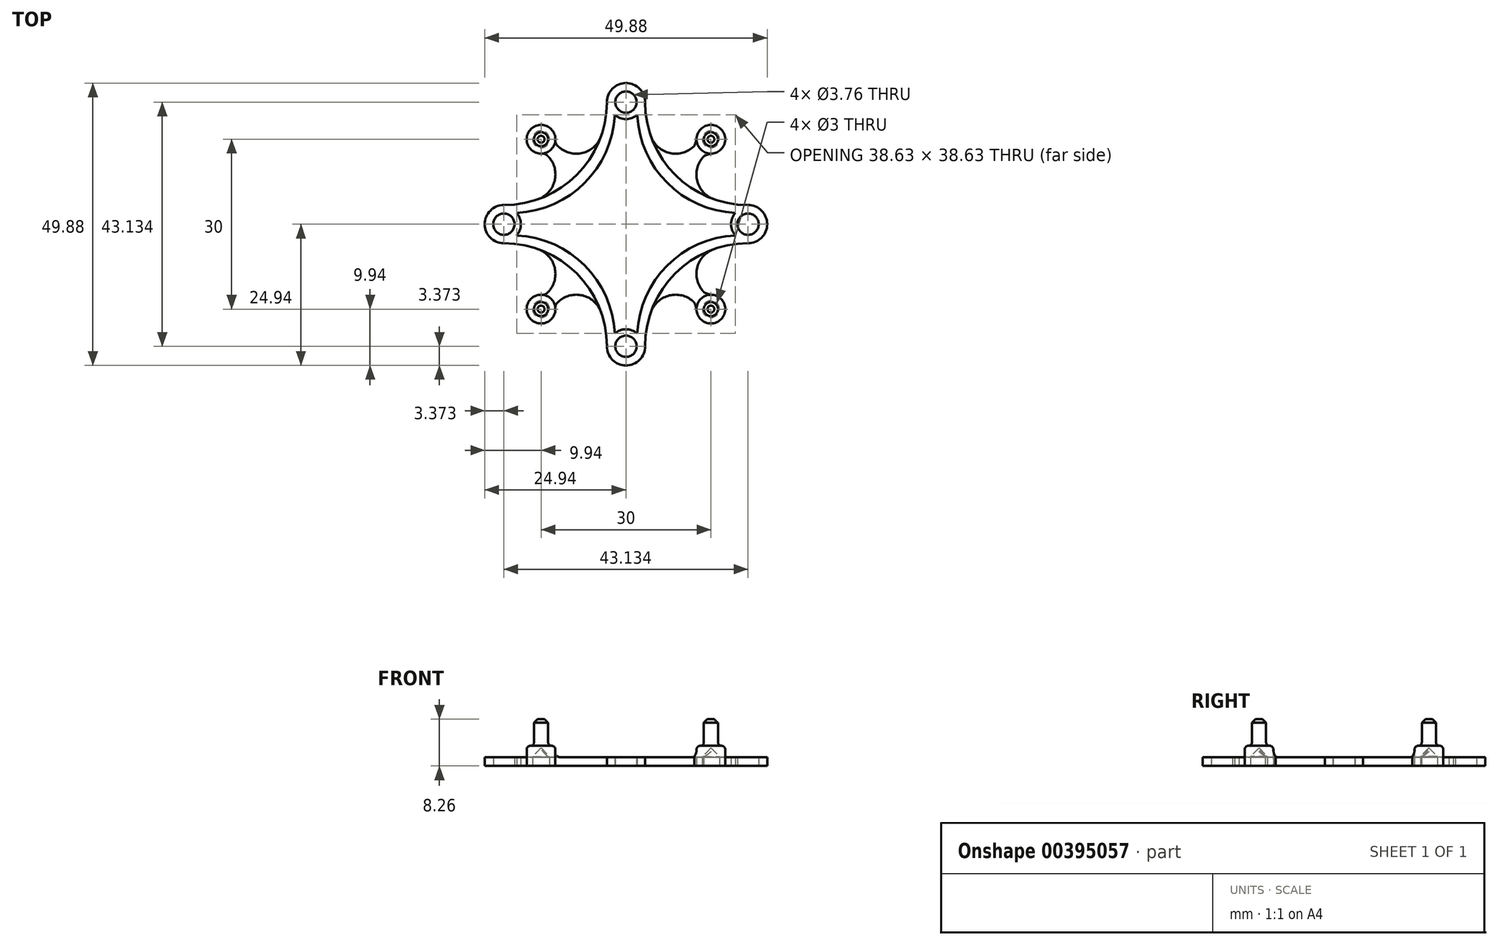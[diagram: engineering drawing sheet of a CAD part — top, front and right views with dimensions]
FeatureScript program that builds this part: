
annotation { "Feature Type Name" : "Feature", "Feature Type Description" : "" }
export const myFeature = defineFeature(function(context is Context, id is Id, definition is map)
    precondition{}
    {
        {
            var Q0;
            Q0=qCreatedBy(makeId("Top.planeOp"),FACE);
            var sketch = newSketch(context, id + "F0", { "sketchPlane" : qUnion([Q0])});
            skCircle(sketch, "E0", {"center": v(0, 21.57) * mm, "radius": 1.88 * mm});
            skCircle(sketch, "E1", {"center": v(-21.57, 0) * mm, "radius": 1.88 * mm});
            skCircle(sketch, "E2", {"center": v(0, -21.57) * mm, "radius": 1.88 * mm});
            skCircle(sketch, "E3", {"center": v(21.57, 0) * mm, "radius": 1.88 * mm});
            skLineSegment(sketch, "E4", {"start": v(0, 21.57) * mm, "end": v(0, -21.57) * mm, "construction": true});
            skLineSegment(sketch, "E5", {"start": v(21.57, 0) * mm, "end": v(-21.57, 0) * mm, "construction": true});
            skArc(sketch, "E6", {"start": v(3.38, 21.57) * mm, "mid": v(0, 24.94) * mm, "end": v(-3.38, 21.57) * mm});
            skArc(sketch, "E7", {"start": v(21.57, -3.38) * mm, "mid": v(24.94, 0) * mm, "end": v(21.57, 3.38) * mm});
            skArc(sketch, "E8", {"start": v(-3.38, -21.57) * mm, "mid": v(0, -24.94) * mm, "end": v(3.38, -21.57) * mm});
            skArc(sketch, "E9", {"start": v(-21.57, 3.38) * mm, "mid": v(-24.94, 0) * mm, "end": v(-21.57, -3.38) * mm});
            skArc(sketch, "E10", {"start": v(21.57, -3.38) * mm, "mid": v(8.7, -8.7) * mm, "end": v(3.38, -21.57) * mm});
            skArc(sketch, "E11", {"start": v(3.38, 21.57) * mm, "mid": v(8.7, 8.7) * mm, "end": v(21.57, 3.38) * mm});
            skArc(sketch, "E12", {"start": v(-21.57, 3.38) * mm, "mid": v(-8.7, 8.7) * mm, "end": v(-3.38, 21.57) * mm});
            skArc(sketch, "E13", {"start": v(-3.38, -21.57) * mm, "mid": v(-8.7, -8.7) * mm, "end": v(-21.57, -3.38) * mm});
            skArc(sketch, "E14", {"start": v(-1.98, 19.32) * mm, "mid": v(0, 18.57) * mm, "end": v(1.98, 19.32) * mm});
            skArc(sketch, "E15", {"start": v(-19.32, -1.98) * mm, "mid": v(-18.57, 0) * mm, "end": v(-19.32, 1.98) * mm});
            skArc(sketch, "E16", {"start": v(1.98, -19.32) * mm, "mid": v(0, -18.57) * mm, "end": v(-1.98, -19.32) * mm});
            skArc(sketch, "E17", {"start": v(19.32, 1.98) * mm, "mid": v(18.57, 0) * mm, "end": v(19.32, -1.98) * mm});
            skArc(sketch, "E18", {"start": v(19.32, -1.98) * mm, "mid": v(7.3, -7.3) * mm, "end": v(1.98, -19.32) * mm});
            skArc(sketch, "E19", {"start": v(1.98, 19.32) * mm, "mid": v(7.3, 7.3) * mm, "end": v(19.32, 1.98) * mm});
            skArc(sketch, "E20", {"start": v(-19.32, 1.98) * mm, "mid": v(-7.3, 7.3) * mm, "end": v(-1.98, 19.32) * mm});
            skArc(sketch, "E21", {"start": v(-1.98, -19.32) * mm, "mid": v(-7.3, -7.3) * mm, "end": v(-19.32, -1.98) * mm});
            skSolve(sketch);
        }
        {
            var Q0;
            Q0=makeQuery(id+"F0.imprint","IMPRINT",FACE,{"disambiguationData":[TD([[makeQuery(id+"F0.imprint","IMPRINT",EDGE,{"derivedFrom":sQuery(id+"F0.wireOp",EDGE,"E0")}),-1.0]])]});
            extrude(context, id + "F1", {"entities" : qUnion([Q0]), "depth" : 0.01 * mm});
        }
        {
            var Q0;
            Q0=qCreatedBy(makeId("Top.planeOp"),FACE);
            var sketch = newSketch(context, id + "F2", { "sketchPlane" : qUnion([Q0])});
            skLineSegment(sketch, "E22.bottom", {"start": v(15, -15) * mm, "end": v(-15, -15) * mm, "construction": true});
            skLineSegment(sketch, "E22.top", {"start": v(15, 15) * mm, "end": v(-15, 15) * mm, "construction": true});
            skLineSegment(sketch, "E22.left", {"start": v(15, -15) * mm, "end": v(15, 15) * mm, "construction": true});
            skLineSegment(sketch, "E22.right", {"start": v(-15, -15) * mm, "end": v(-15, 15) * mm, "construction": true});
            skPoint(sketch, "E22.middle", {"position": v(0, 0) * mm});
            skCircle(sketch, "E23", {"center": v(15, 15) * mm, "radius": 1.25 * mm});
            skCircle(sketch, "E24", {"center": v(15, -15) * mm, "radius": 1.25 * mm});
            skCircle(sketch, "E25", {"center": v(-15, 15) * mm, "radius": 1.25 * mm});
            skCircle(sketch, "E26", {"center": v(-15, -15) * mm, "radius": 1.25 * mm});
            skSolve(sketch);
        }
        {
            var Q0;
            Q0=makeQuery(id+"F2.imprint","IMPRINT",FACE,{"disambiguationData":[TD([[makeQuery(id+"F2.imprint","IMPRINT",EDGE,{"derivedFrom":sQuery(id+"F2.wireOp",EDGE,"E23")}),1.0]])]});
            var Q1;
            Q1=makeQuery(id+"F2.imprint","IMPRINT",FACE,{"disambiguationData":[TD([[makeQuery(id+"F2.imprint","IMPRINT",EDGE,{"derivedFrom":sQuery(id+"F2.wireOp",EDGE,"E25")}),1.0]])]});
            var Q2;
            Q2=makeQuery(id+"F2.imprint","IMPRINT",FACE,{"disambiguationData":[TD([[makeQuery(id+"F2.imprint","IMPRINT",EDGE,{"derivedFrom":sQuery(id+"F2.wireOp",EDGE,"E24")}),1.0]])]});
            var Q3;
            Q3=makeQuery(id+"F2.imprint","IMPRINT",FACE,{"disambiguationData":[TD([[makeQuery(id+"F2.imprint","IMPRINT",EDGE,{"derivedFrom":sQuery(id+"F2.wireOp",EDGE,"E26")}),1.0]])]});
            extrude(context, id + "F3", {"entities" : qUnion([Q0, Q1, Q2, Q3]), "depth" : 8.25 * mm});
        }
        {
            var Q0;
            Q0=qCreatedBy(makeId("Top.planeOp"),FACE);
            var sketch = newSketch(context, id + "F4", { "sketchPlane" : qUnion([Q0])});
            skLineSegment(sketch, "E27", {"start": v(-14.12, 15.88) * mm, "end": v(-6.44, 8.2) * mm});
            skLineSegment(sketch, "E28", {"start": v(-6.44, 8.2) * mm, "end": v(-8.2, 6.44) * mm});
            skLineSegment(sketch, "E29", {"start": v(-8.2, 6.44) * mm, "end": v(-15.88, 14.12) * mm});
            skLineSegment(sketch, "E30", {"start": v(-15.88, 14.12) * mm, "end": v(-14.12, 15.88) * mm});
            skLineSegment(sketch, "E31", {"start": v(14.12, 15.88) * mm, "end": v(15.88, 14.12) * mm});
            skLineSegment(sketch, "E32", {"start": v(15.88, 14.12) * mm, "end": v(8.2, 6.44) * mm});
            skLineSegment(sketch, "E33", {"start": v(8.2, 6.44) * mm, "end": v(6.44, 8.2) * mm});
            skLineSegment(sketch, "E34", {"start": v(6.44, 8.2) * mm, "end": v(14.12, 15.88) * mm});
            skLineSegment(sketch, "E35", {"start": v(8.2, -6.44) * mm, "end": v(15.88, -14.12) * mm});
            skLineSegment(sketch, "E36", {"start": v(15.88, -14.12) * mm, "end": v(14.12, -15.88) * mm});
            skLineSegment(sketch, "E37", {"start": v(14.12, -15.88) * mm, "end": v(6.44, -8.2) * mm});
            skLineSegment(sketch, "E38", {"start": v(6.44, -8.2) * mm, "end": v(8.2, -6.44) * mm});
            skLineSegment(sketch, "E39", {"start": v(-15.88, -14.12) * mm, "end": v(-14.12, -15.88) * mm});
            skLineSegment(sketch, "E40", {"start": v(-14.12, -15.88) * mm, "end": v(-6.44, -8.2) * mm});
            skLineSegment(sketch, "E41", {"start": v(-6.44, -8.2) * mm, "end": v(-8.2, -6.44) * mm});
            skLineSegment(sketch, "E42", {"start": v(-8.2, -6.44) * mm, "end": v(-15.88, -14.12) * mm});
            skLineSegment(sketch, "E43", {"start": v(-7.32, -7.32) * mm, "end": v(0, 0) * mm, "construction": true});
            skLineSegment(sketch, "E44", {"start": v(0, 0) * mm, "end": v(7.32, 7.32) * mm, "construction": true});
            skLineSegment(sketch, "E45", {"start": v(-7.32, 7.32) * mm, "end": v(0, 0) * mm, "construction": true});
            skLineSegment(sketch, "E46", {"start": v(7.32, -7.32) * mm, "end": v(0, 0) * mm, "construction": true});
            skSolve(sketch);
        }
        {
            var Q0;
            Q0=makeQuery(id+"F4.imprint","IMPRINT",FACE,{"disambiguationData":[TD([[makeQuery(id+"F4.imprint","IMPRINT",EDGE,{"derivedFrom":sQuery(id+"F4.wireOp",EDGE,"E31")}),-1.0]])]});
            var Q1;
            Q1=makeQuery(id+"F4.imprint","IMPRINT",FACE,{"disambiguationData":[TD([[makeQuery(id+"F4.imprint","IMPRINT",EDGE,{"derivedFrom":sQuery(id+"F4.wireOp",EDGE,"E27")}),-1.0]])]});
            var Q2;
            Q2=makeQuery(id+"F4.imprint","IMPRINT",FACE,{"disambiguationData":[TD([[makeQuery(id+"F4.imprint","IMPRINT",EDGE,{"derivedFrom":sQuery(id+"F4.wireOp",EDGE,"E35")}),-1.0]])]});
            var Q3;
            Q3=makeQuery(id+"F4.imprint","IMPRINT",FACE,{"disambiguationData":[TD([[makeQuery(id+"F4.imprint","IMPRINT",EDGE,{"derivedFrom":sQuery(id+"F4.wireOp",EDGE,"E39")}),1.0]])]});
            var Q4;
            Q4=makeQuery(id+"F1.opExtrude","CAP_FACE",FACE,{"disambiguationData":[OSD([sQuery(id+"F0.wireOp",EDGE,"E0"),sQuery(id+"F0.wireOp",EDGE,"E1"),sQuery(id+"F0.wireOp",EDGE,"E2"),sQuery(id+"F0.wireOp",EDGE,"E3"),sQuery(id+"F0.wireOp",EDGE,"E6"),sQuery(id+"F0.wireOp",EDGE,"E7"),sQuery(id+"F0.wireOp",EDGE,"E8"),sQuery(id+"F0.wireOp",EDGE,"E9"),sQuery(id+"F0.wireOp",EDGE,"E10"),sQuery(id+"F0.wireOp",EDGE,"E11"),sQuery(id+"F0.wireOp",EDGE,"E12"),sQuery(id+"F0.wireOp",EDGE,"E13"),sQuery(id+"F0.wireOp",EDGE,"E14"),sQuery(id+"F0.wireOp",EDGE,"E15"),sQuery(id+"F0.wireOp",EDGE,"E16"),sQuery(id+"F0.wireOp",EDGE,"E17"),sQuery(id+"F0.wireOp",EDGE,"E18"),sQuery(id+"F0.wireOp",EDGE,"E19"),sQuery(id+"F0.wireOp",EDGE,"E20"),sQuery(id+"F0.wireOp",EDGE,"E21")])],"isStart":false});
            extrude(context, id + "F5", {"entities" : qUnion([Q0, Q1, Q2, Q3, Q4]), "operationType" : NewBodyOperationType.ADD, "depth" : 1.52 * mm});
        }
        {
            var Q0;
            {var subQ0=sQuery(id+"F0.wireOp",EDGE,"E10");Q0=makeQuery(id+"F5.boolean.opBoolean","INTERSECT",EDGE,{"derivedFrom":[makeQuery(id+"F1.opExtrude","SWEPT_FACE",FACE,{"disambiguationData":[OSD([subQ0])]}),makeQuery(id+"F5.opExtrude","SWEPT_FACE",FACE,{"disambiguationData":[OSD([subQ0])]}),makeQuery(id+"F5.opExtrude","SWEPT_FACE",FACE,{"disambiguationData":[OSD([sQuery(id+"F4.wireOp",EDGE,"E37")])]})]});}
            var Q1;
            {var subQ0=sQuery(id+"F0.wireOp",EDGE,"E10");Q1=makeQuery(id+"F5.boolean.opBoolean","INTERSECT",EDGE,{"derivedFrom":[makeQuery(id+"F1.opExtrude","SWEPT_FACE",FACE,{"disambiguationData":[OSD([subQ0])]}),makeQuery(id+"F5.opExtrude","SWEPT_FACE",FACE,{"disambiguationData":[OSD([subQ0])]}),makeQuery(id+"F5.opExtrude","SWEPT_FACE",FACE,{"disambiguationData":[OSD([sQuery(id+"F4.wireOp",EDGE,"E35")])]})]});}
            var Q2;
            {var subQ0=sQuery(id+"F0.wireOp",EDGE,"E11");Q2=makeQuery(id+"F5.boolean.opBoolean","INTERSECT",EDGE,{"derivedFrom":[makeQuery(id+"F1.opExtrude","SWEPT_FACE",FACE,{"disambiguationData":[OSD([subQ0])]}),makeQuery(id+"F5.opExtrude","SWEPT_FACE",FACE,{"disambiguationData":[OSD([subQ0])]}),makeQuery(id+"F5.opExtrude","SWEPT_FACE",FACE,{"disambiguationData":[OSD([sQuery(id+"F4.wireOp",EDGE,"E32")])]})]});}
            var Q3;
            {var subQ0=sQuery(id+"F0.wireOp",EDGE,"E11");Q3=makeQuery(id+"F5.boolean.opBoolean","INTERSECT",EDGE,{"derivedFrom":[makeQuery(id+"F1.opExtrude","SWEPT_FACE",FACE,{"disambiguationData":[OSD([subQ0])]}),makeQuery(id+"F5.opExtrude","SWEPT_FACE",FACE,{"disambiguationData":[OSD([subQ0])]}),makeQuery(id+"F5.opExtrude","SWEPT_FACE",FACE,{"disambiguationData":[OSD([sQuery(id+"F4.wireOp",EDGE,"E34")])]})]});}
            var Q4;
            {var subQ0=sQuery(id+"F0.wireOp",EDGE,"E12");Q4=makeQuery(id+"F5.boolean.opBoolean","INTERSECT",EDGE,{"derivedFrom":[makeQuery(id+"F1.opExtrude","SWEPT_FACE",FACE,{"disambiguationData":[OSD([subQ0])]}),makeQuery(id+"F5.opExtrude","SWEPT_FACE",FACE,{"disambiguationData":[OSD([subQ0])]}),makeQuery(id+"F5.opExtrude","SWEPT_FACE",FACE,{"disambiguationData":[OSD([sQuery(id+"F4.wireOp",EDGE,"E27")])]})]});}
            var Q5;
            {var subQ0=sQuery(id+"F0.wireOp",EDGE,"E12");Q5=makeQuery(id+"F5.boolean.opBoolean","INTERSECT",EDGE,{"derivedFrom":[makeQuery(id+"F1.opExtrude","SWEPT_FACE",FACE,{"disambiguationData":[OSD([subQ0])]}),makeQuery(id+"F5.opExtrude","SWEPT_FACE",FACE,{"disambiguationData":[OSD([subQ0])]}),makeQuery(id+"F5.opExtrude","SWEPT_FACE",FACE,{"disambiguationData":[OSD([sQuery(id+"F4.wireOp",EDGE,"E29")])]})]});}
            var Q6;
            {var subQ0=sQuery(id+"F0.wireOp",EDGE,"E13");Q6=makeQuery(id+"F5.boolean.opBoolean","INTERSECT",EDGE,{"derivedFrom":[makeQuery(id+"F1.opExtrude","SWEPT_FACE",FACE,{"disambiguationData":[OSD([subQ0])]}),makeQuery(id+"F5.opExtrude","SWEPT_FACE",FACE,{"disambiguationData":[OSD([subQ0])]}),makeQuery(id+"F5.opExtrude","SWEPT_FACE",FACE,{"disambiguationData":[OSD([sQuery(id+"F4.wireOp",EDGE,"E42")])]})]});}
            var Q7;
            {var subQ0=sQuery(id+"F0.wireOp",EDGE,"E13");Q7=makeQuery(id+"F5.boolean.opBoolean","INTERSECT",EDGE,{"derivedFrom":[makeQuery(id+"F1.opExtrude","SWEPT_FACE",FACE,{"disambiguationData":[OSD([subQ0])]}),makeQuery(id+"F5.opExtrude","SWEPT_FACE",FACE,{"disambiguationData":[OSD([subQ0])]}),makeQuery(id+"F5.opExtrude","SWEPT_FACE",FACE,{"disambiguationData":[OSD([sQuery(id+"F4.wireOp",EDGE,"E40")])]})]});}
            fillet(context, id + "F6", {"entities" : qUnion([Q0, Q1, Q2, Q3, Q4, Q5, Q6, Q7]), "radius" : 4.64 * mm, "tangentPropagation" : true, "allowEdgeOverflow" : false});
        }
        {
            var Q0;
            Q0=makeQuery(id+"F5.boolean.opBoolean","MERGE",FACE,{"derivedFrom":[makeQuery(id+"F1.opExtrude","CAP_FACE",FACE,{"disambiguationData":[OSD([sQuery(id+"F0.wireOp",EDGE,"E0"),sQuery(id+"F0.wireOp",EDGE,"E1"),sQuery(id+"F0.wireOp",EDGE,"E2"),sQuery(id+"F0.wireOp",EDGE,"E3"),sQuery(id+"F0.wireOp",EDGE,"E6"),sQuery(id+"F0.wireOp",EDGE,"E7"),sQuery(id+"F0.wireOp",EDGE,"E8"),sQuery(id+"F0.wireOp",EDGE,"E9"),sQuery(id+"F0.wireOp",EDGE,"E10"),sQuery(id+"F0.wireOp",EDGE,"E11"),sQuery(id+"F0.wireOp",EDGE,"E12"),sQuery(id+"F0.wireOp",EDGE,"E13"),sQuery(id+"F0.wireOp",EDGE,"E14"),sQuery(id+"F0.wireOp",EDGE,"E15"),sQuery(id+"F0.wireOp",EDGE,"E16"),sQuery(id+"F0.wireOp",EDGE,"E17"),sQuery(id+"F0.wireOp",EDGE,"E18"),sQuery(id+"F0.wireOp",EDGE,"E19"),sQuery(id+"F0.wireOp",EDGE,"E20"),sQuery(id+"F0.wireOp",EDGE,"E21")])],"isStart":true}),makeQuery(id+"F3.opExtrude","CAP_FACE",FACE,{"disambiguationData":[OSD([sQuery(id+"F2.wireOp",EDGE,"E23")])],"isStart":true}),makeQuery(id+"F3.opExtrude","CAP_FACE",FACE,{"disambiguationData":[OSD([sQuery(id+"F2.wireOp",EDGE,"E24")])],"isStart":true}),makeQuery(id+"F3.opExtrude","CAP_FACE",FACE,{"disambiguationData":[OSD([sQuery(id+"F2.wireOp",EDGE,"E25")])],"isStart":true}),makeQuery(id+"F3.opExtrude","CAP_FACE",FACE,{"disambiguationData":[OSD([sQuery(id+"F2.wireOp",EDGE,"E26")])],"isStart":true}),makeQuery(id+"F5.opExtrude","CAP_FACE",FACE,{"disambiguationData":[OSD([sQuery(id+"F4.wireOp",EDGE,"E27"),sQuery(id+"F4.wireOp",EDGE,"E28"),sQuery(id+"F4.wireOp",EDGE,"E29"),sQuery(id+"F4.wireOp",EDGE,"E30")])],"isStart":true}),makeQuery(id+"F5.opExtrude","CAP_FACE",FACE,{"disambiguationData":[OSD([sQuery(id+"F4.wireOp",EDGE,"E31"),sQuery(id+"F4.wireOp",EDGE,"E32"),sQuery(id+"F4.wireOp",EDGE,"E33"),sQuery(id+"F4.wireOp",EDGE,"E34")])],"isStart":true}),makeQuery(id+"F5.opExtrude","CAP_FACE",FACE,{"disambiguationData":[OSD([sQuery(id+"F4.wireOp",EDGE,"E35"),sQuery(id+"F4.wireOp",EDGE,"E36"),sQuery(id+"F4.wireOp",EDGE,"E37"),sQuery(id+"F4.wireOp",EDGE,"E38")])],"isStart":true}),makeQuery(id+"F5.opExtrude","CAP_FACE",FACE,{"disambiguationData":[OSD([sQuery(id+"F4.wireOp",EDGE,"E39"),sQuery(id+"F4.wireOp",EDGE,"E40"),sQuery(id+"F4.wireOp",EDGE,"E41"),sQuery(id+"F4.wireOp",EDGE,"E42")])],"isStart":true})]});
            var sketch = newSketch(context, id + "F7", { "sketchPlane" : qUnion([Q0])});
            skCircle(sketch, "E47", {"center": v(15, 15) * mm, "radius": 2.53 * mm});
            skCircle(sketch, "E48", {"center": v(15, -15) * mm, "radius": 2.53 * mm});
            skCircle(sketch, "E49", {"center": v(-15, -15) * mm, "radius": 2.53 * mm});
            skCircle(sketch, "E50", {"center": v(-15, 15) * mm, "radius": 2.53 * mm});
            skSolve(sketch);
        }
        {
            var Q0;
            Q0 = qSketchRegion(id + "F7", true);
            extrude(context, id + "F8", {"entities" : qUnion([Q0]), "operationType" : NewBodyOperationType.ADD, "oppositeDirection" : true, "depth" : 3.56 * mm});
        }
        {
            var Q0;
            Q0=makeQuery(id+"F8.opExtrude","CAP_EDGE",EDGE,{"disambiguationData":[OSD([sQuery(id+"F7.wireOp",EDGE,"E49")])],"isStart":false});
            var Q1;
            Q1=makeQuery(id+"F8.opExtrude","CAP_EDGE",EDGE,{"disambiguationData":[OSD([sQuery(id+"F7.wireOp",EDGE,"E48")])],"isStart":false});
            var Q2;
            Q2=makeQuery(id+"F8.opExtrude","CAP_EDGE",EDGE,{"disambiguationData":[OSD([sQuery(id+"F7.wireOp",EDGE,"E47")])],"isStart":false});
            var Q3;
            Q3=makeQuery(id+"F8.opExtrude","CAP_EDGE",EDGE,{"disambiguationData":[OSD([sQuery(id+"F7.wireOp",EDGE,"E50")])],"isStart":false});
            fillet(context, id + "F9", {"entities" : qUnion([Q0, Q1, Q2, Q3]), "radius" : 0.64 * mm, "tangentPropagation" : true, "allowEdgeOverflow" : false});
        }
        {
            var Q0;
            Q0=makeQuery(id+"F8.boolean.opBoolean","INTERSECT",EDGE,{"derivedFrom":[makeQuery(id+"F3.opExtrude","SWEPT_FACE",FACE,{"disambiguationData":[OSD([sQuery(id+"F2.wireOp",EDGE,"E25")])]}),makeQuery(id+"F8.opExtrude","CAP_FACE",FACE,{"disambiguationData":[OSD([sQuery(id+"F7.wireOp",EDGE,"E49")])],"isStart":false})]});
            var Q1;
            Q1=makeQuery(id+"F8.boolean.opBoolean","INTERSECT",EDGE,{"derivedFrom":[makeQuery(id+"F3.opExtrude","SWEPT_FACE",FACE,{"disambiguationData":[OSD([sQuery(id+"F2.wireOp",EDGE,"E23")])]}),makeQuery(id+"F8.opExtrude","CAP_FACE",FACE,{"disambiguationData":[OSD([sQuery(id+"F7.wireOp",EDGE,"E48")])],"isStart":false})]});
            var Q2;
            Q2=makeQuery(id+"F8.boolean.opBoolean","INTERSECT",EDGE,{"derivedFrom":[makeQuery(id+"F3.opExtrude","SWEPT_FACE",FACE,{"disambiguationData":[OSD([sQuery(id+"F2.wireOp",EDGE,"E24")])]}),makeQuery(id+"F8.opExtrude","CAP_FACE",FACE,{"disambiguationData":[OSD([sQuery(id+"F7.wireOp",EDGE,"E47")])],"isStart":false})]});
            var Q3;
            Q3=makeQuery(id+"F8.boolean.opBoolean","INTERSECT",EDGE,{"derivedFrom":[makeQuery(id+"F3.opExtrude","SWEPT_FACE",FACE,{"disambiguationData":[OSD([sQuery(id+"F2.wireOp",EDGE,"E26")])]}),makeQuery(id+"F8.opExtrude","CAP_FACE",FACE,{"disambiguationData":[OSD([sQuery(id+"F7.wireOp",EDGE,"E50")])],"isStart":false})]});
            fillet(context, id + "F10", {"entities" : qUnion([Q0, Q1, Q2, Q3]), "radius" : 0.64 * mm, "tangentPropagation" : true, "allowEdgeOverflow" : false});
        }
        {
            var Q0;
            Q0=makeQuery(id+"F3.opExtrude","CAP_EDGE",EDGE,{"disambiguationData":[OSD([sQuery(id+"F2.wireOp",EDGE,"E25")])],"isStart":false});
            var Q1;
            Q1=makeQuery(id+"F3.opExtrude","CAP_EDGE",EDGE,{"disambiguationData":[OSD([sQuery(id+"F2.wireOp",EDGE,"E26")])],"isStart":false});
            var Q2;
            Q2=makeQuery(id+"F3.opExtrude","CAP_EDGE",EDGE,{"disambiguationData":[OSD([sQuery(id+"F2.wireOp",EDGE,"E24")])],"isStart":false});
            var Q3;
            Q3=makeQuery(id+"F3.opExtrude","CAP_EDGE",EDGE,{"disambiguationData":[OSD([sQuery(id+"F2.wireOp",EDGE,"E23")])],"isStart":false});
            chamfer(context, id + "F11", {"entities" : qUnion([Q0, Q1, Q2, Q3]), "width" : 0.64 * mm, "tangentPropagation" : true});
        }
        {
            var Q0;
            Q0=makeQuery(id+"F8.boolean.opBoolean","INTERSECT",EDGE,{"derivedFrom":[makeQuery(id+"F5.opExtrude","SWEPT_FACE",FACE,{"disambiguationData":[OSD([sQuery(id+"F4.wireOp",EDGE,"E34")])]}),makeQuery(id+"F8.opExtrude","SWEPT_FACE",FACE,{"disambiguationData":[OSD([sQuery(id+"F7.wireOp",EDGE,"E48")])]})]});
            var Q1;
            Q1=makeQuery(id+"F8.boolean.opBoolean","INTERSECT",EDGE,{"derivedFrom":[makeQuery(id+"F5.opExtrude","SWEPT_FACE",FACE,{"disambiguationData":[OSD([sQuery(id+"F4.wireOp",EDGE,"E32")])]}),makeQuery(id+"F8.opExtrude","SWEPT_FACE",FACE,{"disambiguationData":[OSD([sQuery(id+"F7.wireOp",EDGE,"E48")])]})]});
            fillet(context, id + "F12", {"entities" : qUnion([Q0, Q1]), "radius" : 5.08 * mm, "tangentPropagation" : true, "allowEdgeOverflow" : false});
        }
        {
            var Q0;
            Q0=makeQuery(id+"F8.boolean.opBoolean","INTERSECT",EDGE,{"derivedFrom":[makeQuery(id+"F5.opExtrude","CAP_FACE",FACE,{"disambiguationData":[OSD([sQuery(id+"F4.wireOp",EDGE,"E31"),sQuery(id+"F4.wireOp",EDGE,"E32"),sQuery(id+"F4.wireOp",EDGE,"E33"),sQuery(id+"F4.wireOp",EDGE,"E34")])],"isStart":false}),makeQuery(id+"F8.opExtrude","SWEPT_FACE",FACE,{"disambiguationData":[OSD([sQuery(id+"F7.wireOp",EDGE,"E48")])]})]});
            fillet(context, id + "F13", {"entities" : qUnion([Q0]), "radius" : 1.27 * mm, "tangentPropagation" : true, "allowEdgeOverflow" : false});
        }
        {
            var Q0;
            Q0=makeQuery(id+"F8.boolean.opBoolean","INTERSECT",EDGE,{"derivedFrom":[makeQuery(id+"F5.opExtrude","SWEPT_FACE",FACE,{"disambiguationData":[OSD([sQuery(id+"F4.wireOp",EDGE,"E35")])]}),makeQuery(id+"F8.opExtrude","SWEPT_FACE",FACE,{"disambiguationData":[OSD([sQuery(id+"F7.wireOp",EDGE,"E47")])]})]});
            var Q1;
            Q1=makeQuery(id+"F8.boolean.opBoolean","INTERSECT",EDGE,{"derivedFrom":[makeQuery(id+"F5.opExtrude","SWEPT_FACE",FACE,{"disambiguationData":[OSD([sQuery(id+"F4.wireOp",EDGE,"E37")])]}),makeQuery(id+"F8.opExtrude","SWEPT_FACE",FACE,{"disambiguationData":[OSD([sQuery(id+"F7.wireOp",EDGE,"E47")])]})]});
            fillet(context, id + "F14", {"entities" : qUnion([Q0, Q1]), "radius" : 5.08 * mm, "tangentPropagation" : true, "allowEdgeOverflow" : false});
        }
        {
            var Q0;
            Q0=makeQuery(id+"F8.boolean.opBoolean","INTERSECT",EDGE,{"derivedFrom":[makeQuery(id+"F5.opExtrude","CAP_FACE",FACE,{"disambiguationData":[OSD([sQuery(id+"F4.wireOp",EDGE,"E35"),sQuery(id+"F4.wireOp",EDGE,"E36"),sQuery(id+"F4.wireOp",EDGE,"E37"),sQuery(id+"F4.wireOp",EDGE,"E38")])],"isStart":false}),makeQuery(id+"F8.opExtrude","SWEPT_FACE",FACE,{"disambiguationData":[OSD([sQuery(id+"F7.wireOp",EDGE,"E47")])]})]});
            var Q1;
            Q1=makeQuery(id+"F8.boolean.opBoolean","INTERSECT",EDGE,{"derivedFrom":[makeQuery(id+"F5.opExtrude","SWEPT_FACE",FACE,{"disambiguationData":[OSD([sQuery(id+"F4.wireOp",EDGE,"E42")])]}),makeQuery(id+"F8.opExtrude","SWEPT_FACE",FACE,{"disambiguationData":[OSD([sQuery(id+"F7.wireOp",EDGE,"E50")])]})]});
            var Q2;
            Q2=makeQuery(id+"F8.boolean.opBoolean","INTERSECT",EDGE,{"derivedFrom":[makeQuery(id+"F5.opExtrude","SWEPT_FACE",FACE,{"disambiguationData":[OSD([sQuery(id+"F4.wireOp",EDGE,"E40")])]}),makeQuery(id+"F8.opExtrude","SWEPT_FACE",FACE,{"disambiguationData":[OSD([sQuery(id+"F7.wireOp",EDGE,"E50")])]})]});
            var Q3;
            Q3=makeQuery(id+"F8.boolean.opBoolean","INTERSECT",EDGE,{"derivedFrom":[makeQuery(id+"F5.opExtrude","SWEPT_FACE",FACE,{"disambiguationData":[OSD([sQuery(id+"F4.wireOp",EDGE,"E27")])]}),makeQuery(id+"F8.opExtrude","SWEPT_FACE",FACE,{"disambiguationData":[OSD([sQuery(id+"F7.wireOp",EDGE,"E49")])]})]});
            var Q4;
            Q4=makeQuery(id+"F8.boolean.opBoolean","INTERSECT",EDGE,{"derivedFrom":[makeQuery(id+"F5.opExtrude","SWEPT_FACE",FACE,{"disambiguationData":[OSD([sQuery(id+"F4.wireOp",EDGE,"E29")])]}),makeQuery(id+"F8.opExtrude","SWEPT_FACE",FACE,{"disambiguationData":[OSD([sQuery(id+"F7.wireOp",EDGE,"E49")])]})]});
            fillet(context, id + "F15", {"entities" : qUnion([Q0, Q1, Q2, Q3, Q4]), "radius" : 1.27 * mm, "tangentPropagation" : true, "allowEdgeOverflow" : false});
        }
        {
            var Q0;
            Q0=makeQuery(id+"F8.boolean.opBoolean","INTERSECT",EDGE,{"derivedFrom":[makeQuery(id+"F5.opExtrude","CAP_FACE",FACE,{"disambiguationData":[OSD([sQuery(id+"F4.wireOp",EDGE,"E39"),sQuery(id+"F4.wireOp",EDGE,"E40"),sQuery(id+"F4.wireOp",EDGE,"E41"),sQuery(id+"F4.wireOp",EDGE,"E42")])],"isStart":false}),makeQuery(id+"F8.opExtrude","SWEPT_FACE",FACE,{"disambiguationData":[OSD([sQuery(id+"F7.wireOp",EDGE,"E50")])]})]});
            var Q1;
            Q1=makeQuery(id+"F8.boolean.opBoolean","INTERSECT",EDGE,{"derivedFrom":[makeQuery(id+"F5.opExtrude","CAP_FACE",FACE,{"disambiguationData":[OSD([sQuery(id+"F4.wireOp",EDGE,"E27"),sQuery(id+"F4.wireOp",EDGE,"E28"),sQuery(id+"F4.wireOp",EDGE,"E29"),sQuery(id+"F4.wireOp",EDGE,"E30")])],"isStart":false}),makeQuery(id+"F8.opExtrude","SWEPT_FACE",FACE,{"disambiguationData":[OSD([sQuery(id+"F7.wireOp",EDGE,"E49")])]})]});
            fillet(context, id + "F16", {"entities" : qUnion([Q0, Q1]), "radius" : 1.27 * mm, "tangentPropagation" : true, "allowEdgeOverflow" : false});
        }
        {
            var Q0;
            Q0=makeQuery(id+"F8.boolean.opBoolean","MERGE",FACE,{"derivedFrom":[makeQuery(id+"F5.boolean.opBoolean","MERGE",FACE,{"derivedFrom":[makeQuery(id+"F1.opExtrude","CAP_FACE",FACE,{"disambiguationData":[OSD([sQuery(id+"F0.wireOp",EDGE,"E0"),sQuery(id+"F0.wireOp",EDGE,"E1"),sQuery(id+"F0.wireOp",EDGE,"E2"),sQuery(id+"F0.wireOp",EDGE,"E3"),sQuery(id+"F0.wireOp",EDGE,"E6"),sQuery(id+"F0.wireOp",EDGE,"E7"),sQuery(id+"F0.wireOp",EDGE,"E8"),sQuery(id+"F0.wireOp",EDGE,"E9"),sQuery(id+"F0.wireOp",EDGE,"E10"),sQuery(id+"F0.wireOp",EDGE,"E11"),sQuery(id+"F0.wireOp",EDGE,"E12"),sQuery(id+"F0.wireOp",EDGE,"E13"),sQuery(id+"F0.wireOp",EDGE,"E14"),sQuery(id+"F0.wireOp",EDGE,"E15"),sQuery(id+"F0.wireOp",EDGE,"E16"),sQuery(id+"F0.wireOp",EDGE,"E17"),sQuery(id+"F0.wireOp",EDGE,"E18"),sQuery(id+"F0.wireOp",EDGE,"E19"),sQuery(id+"F0.wireOp",EDGE,"E20"),sQuery(id+"F0.wireOp",EDGE,"E21")])],"isStart":true}),makeQuery(id+"F3.opExtrude","CAP_FACE",FACE,{"disambiguationData":[OSD([sQuery(id+"F2.wireOp",EDGE,"E23")])],"isStart":true}),makeQuery(id+"F3.opExtrude","CAP_FACE",FACE,{"disambiguationData":[OSD([sQuery(id+"F2.wireOp",EDGE,"E24")])],"isStart":true}),makeQuery(id+"F3.opExtrude","CAP_FACE",FACE,{"disambiguationData":[OSD([sQuery(id+"F2.wireOp",EDGE,"E25")])],"isStart":true}),makeQuery(id+"F3.opExtrude","CAP_FACE",FACE,{"disambiguationData":[OSD([sQuery(id+"F2.wireOp",EDGE,"E26")])],"isStart":true}),makeQuery(id+"F5.opExtrude","CAP_FACE",FACE,{"disambiguationData":[OSD([sQuery(id+"F4.wireOp",EDGE,"E27"),sQuery(id+"F4.wireOp",EDGE,"E28"),sQuery(id+"F4.wireOp",EDGE,"E29"),sQuery(id+"F4.wireOp",EDGE,"E30")])],"isStart":true}),makeQuery(id+"F5.opExtrude","CAP_FACE",FACE,{"disambiguationData":[OSD([sQuery(id+"F4.wireOp",EDGE,"E31"),sQuery(id+"F4.wireOp",EDGE,"E32"),sQuery(id+"F4.wireOp",EDGE,"E33"),sQuery(id+"F4.wireOp",EDGE,"E34")])],"isStart":true}),makeQuery(id+"F5.opExtrude","CAP_FACE",FACE,{"disambiguationData":[OSD([sQuery(id+"F4.wireOp",EDGE,"E35"),sQuery(id+"F4.wireOp",EDGE,"E36"),sQuery(id+"F4.wireOp",EDGE,"E37"),sQuery(id+"F4.wireOp",EDGE,"E38")])],"isStart":true}),makeQuery(id+"F5.opExtrude","CAP_FACE",FACE,{"disambiguationData":[OSD([sQuery(id+"F4.wireOp",EDGE,"E39"),sQuery(id+"F4.wireOp",EDGE,"E40"),sQuery(id+"F4.wireOp",EDGE,"E41"),sQuery(id+"F4.wireOp",EDGE,"E42")])],"isStart":true})]}),makeQuery(id+"F8.opExtrude","CAP_FACE",FACE,{"disambiguationData":[OSD([sQuery(id+"F7.wireOp",EDGE,"E47")])],"isStart":true}),makeQuery(id+"F8.opExtrude","CAP_FACE",FACE,{"disambiguationData":[OSD([sQuery(id+"F7.wireOp",EDGE,"E48")])],"isStart":true}),makeQuery(id+"F8.opExtrude","CAP_FACE",FACE,{"disambiguationData":[OSD([sQuery(id+"F7.wireOp",EDGE,"E49")])],"isStart":true}),makeQuery(id+"F8.opExtrude","CAP_FACE",FACE,{"disambiguationData":[OSD([sQuery(id+"F7.wireOp",EDGE,"E50")])],"isStart":true})]});
            var sketch = newSketch(context, id + "F17", { "sketchPlane" : qUnion([Q0])});
            skCircle(sketch, "E51", {"center": v(15, 15) * mm, "radius": 1.5 * mm});
            skCircle(sketch, "E52", {"center": v(15, -15) * mm, "radius": 1.5 * mm});
            skCircle(sketch, "E53", {"center": v(-15, 15) * mm, "radius": 1.5 * mm});
            skCircle(sketch, "E54", {"center": v(-15, -15) * mm, "radius": 1.5 * mm});
            skSolve(sketch);
        }
        {
            var Q0;
            Q0 = qSketchRegion(id + "F17", true);
            extrude(context, id + "F18", {"entities" : qUnion([Q0]), "operationType" : NewBodyOperationType.REMOVE, "oppositeDirection" : true, "depth" : 3.17 * mm});
        }
        {
            var Q0;
            Q0=makeQuery(id+"F18.boolean.opBoolean","COPY",EDGE,{"derivedFrom":makeQuery(id+"F18.opExtrude","CAP_EDGE",EDGE,{"disambiguationData":[OSD([sQuery(id+"F17.wireOp",EDGE,"E54")])],"isStart":false})});
            var Q1;
            Q1=makeQuery(id+"F18.boolean.opBoolean","COPY",EDGE,{"derivedFrom":makeQuery(id+"F18.opExtrude","CAP_EDGE",EDGE,{"disambiguationData":[OSD([sQuery(id+"F17.wireOp",EDGE,"E52")])],"isStart":false})});
            var Q2;
            Q2=makeQuery(id+"F18.boolean.opBoolean","COPY",EDGE,{"derivedFrom":makeQuery(id+"F18.opExtrude","CAP_EDGE",EDGE,{"disambiguationData":[OSD([sQuery(id+"F17.wireOp",EDGE,"E51")])],"isStart":false})});
            var Q3;
            Q3=makeQuery(id+"F18.boolean.opBoolean","COPY",EDGE,{"derivedFrom":makeQuery(id+"F18.opExtrude","CAP_EDGE",EDGE,{"disambiguationData":[OSD([sQuery(id+"F17.wireOp",EDGE,"E53")])],"isStart":false})});
            chamfer(context, id + "F19", {"entities" : qUnion([Q0, Q1, Q2, Q3]), "width" : 1.5 * mm, "tangentPropagation" : true});
        }
    });
